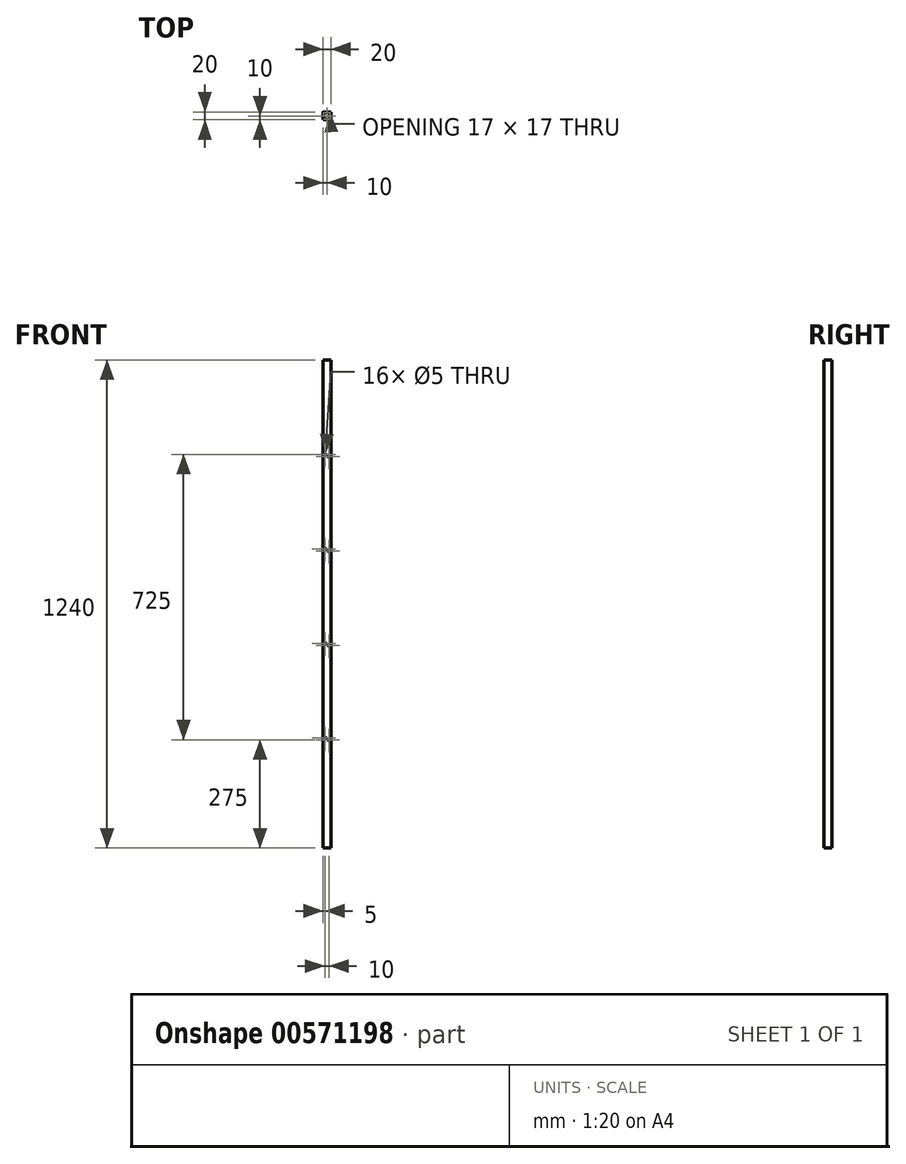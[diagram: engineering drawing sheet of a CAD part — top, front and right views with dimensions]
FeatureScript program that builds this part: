
annotation { "Feature Type Name" : "Feature", "Feature Type Description" : "" }
export const myFeature = defineFeature(function(context is Context, id is Id, definition is map)
    precondition{}
    {
        {
            var Q0;
            Q0=qCreatedBy(makeId("Top.planeOp"),FACE);
            var sketch = newSketch(context, id + "F0", { "sketchPlane" : qUnion([Q0])});
            skLineSegment(sketch, "E0.bottom", {"start": v(0, 0) * mm, "end": v(20, 0) * mm});
            skLineSegment(sketch, "E0.top", {"start": v(0.5, 20) * mm, "end": v(20, 20) * mm});
            skLineSegment(sketch, "E0.left", {"start": v(0, 0) * mm, "end": v(0, 19.5) * mm});
            skLineSegment(sketch, "E0.right", {"start": v(20, 0) * mm, "end": v(20, 20) * mm});
            skLineSegment(sketch, "E1.bottom", {"start": v(2, 18.5) * mm, "end": v(18, 18.5) * mm});
            skLineSegment(sketch, "E1.top", {"start": v(2, 1.5) * mm, "end": v(18, 1.5) * mm});
            skLineSegment(sketch, "E1.left", {"start": v(1.5, 18) * mm, "end": v(1.5, 2) * mm});
            skLineSegment(sketch, "E1.right", {"start": v(18.5, 18) * mm, "end": v(18.5, 2) * mm});
            skPoint(sketch, "E2.visualSharp", {"position": v(1.5, 18.5) * mm});
            skArc(sketch, "E2.filletArc", {"start": v(2, 18.5) * mm, "mid": v(1.65, 18.35) * mm, "end": v(1.5, 18) * mm});
            skPoint(sketch, "E3.visualSharp", {"position": v(1.5, 1.5) * mm});
            skArc(sketch, "E3.filletArc", {"start": v(1.5, 2) * mm, "mid": v(1.65, 1.65) * mm, "end": v(2, 1.5) * mm});
            skPoint(sketch, "E4.visualSharp", {"position": v(18.5, 1.5) * mm});
            skArc(sketch, "E4.filletArc", {"start": v(18, 1.5) * mm, "mid": v(18.35, 1.65) * mm, "end": v(18.5, 2) * mm});
            skPoint(sketch, "E5.visualSharp", {"position": v(18.5, 18.5) * mm});
            skArc(sketch, "E5.filletArc", {"start": v(18.5, 18) * mm, "mid": v(18.35, 18.35) * mm, "end": v(18, 18.5) * mm});
            skPoint(sketch, "E6.visualSharp", {"position": v(0, 20) * mm});
            skArc(sketch, "E6.filletArc", {"start": v(0.5, 20) * mm, "mid": v(0.15, 19.85) * mm, "end": v(0, 19.5) * mm});
            skSolve(sketch);
        }
        {
            var Q0;
            Q0=makeQuery(id+"F0.imprint","IMPRINT",FACE,{"disambiguationData":[TD([[makeQuery(id+"F0.imprint","IMPRINT",EDGE,{"derivedFrom":sQuery(id+"F0.wireOp",EDGE,"E0.bottom")}),1.0]])]});
            extrude(context, id + "F1", {"entities" : qUnion([Q0]), "depth" : 1240 * mm, "offsetDistance" : 25 * mm});
        }
        {
            var Q0;
            Q0=makeQuery(id+"F1.opExtrude","SWEPT_FACE",FACE,{"disambiguationData":[OSD([sQuery(id+"F0.wireOp",EDGE,"E0.bottom")])]});
            var sketch = newSketch(context, id + "F2", { "sketchPlane" : qUnion([Q0])});
            skPoint(sketch, "E7", {"position": v(5, 1000) * mm});
            skPoint(sketch, "E8", {"position": v(15, 995) * mm});
            skPoint(sketch, "E9.0.1.0", {"position": v(15, 755) * mm});
            skPoint(sketch, "E9.0.1.1", {"position": v(5, 760) * mm});
            skPoint(sketch, "E9.0.2.0", {"position": v(15, 515) * mm});
            skPoint(sketch, "E9.0.2.1", {"position": v(5, 520) * mm});
            skPoint(sketch, "E9.0.3.0", {"position": v(15, 275) * mm});
            skPoint(sketch, "E9.0.3.1", {"position": v(5, 280) * mm});
            skLineSegment(sketch, "E9.direction1", {"start": v(5, 1000) * mm, "end": v(30, 1000) * mm, "construction": true});
            skLineSegment(sketch, "E9.direction2", {"start": v(5, 1000) * mm, "end": v(5, 760) * mm, "construction": true});
            skSolve(sketch);
        }
        {
            var Q0;
            Q0=sQuery(id+"F2.wireOp",VERTEX,"E7");
            var Q1;
            Q1=sQuery(id+"F2.wireOp",VERTEX,"E8");
            var Q2;
            Q2=sQuery(id+"F2.wireOp",VERTEX,"E9.0.1.1");
            var Q3;
            Q3=sQuery(id+"F2.wireOp",VERTEX,"E9.0.1.0");
            var Q4;
            Q4=sQuery(id+"F2.wireOp",VERTEX,"E9.0.2.1");
            var Q5;
            Q5=sQuery(id+"F2.wireOp",VERTEX,"E9.0.2.0");
            var Q6;
            Q6=sQuery(id+"F2.wireOp",VERTEX,"E9.0.3.1");
            var Q7;
            Q7=sQuery(id+"F2.wireOp",VERTEX,"E9.0.3.0");
            var Q8;
            Q8=makeQuery(id+"F1.opExtrude","SWEPT_BODY",BODY,{"disambiguationData":[OSD([sQuery(id+"F0.wireOp",EDGE,"E0.bottom"),sQuery(id+"F0.wireOp",EDGE,"E0.top"),sQuery(id+"F0.wireOp",EDGE,"E0.left"),sQuery(id+"F0.wireOp",EDGE,"E0.right"),sQuery(id+"F0.wireOp",EDGE,"E1.bottom"),sQuery(id+"F0.wireOp",EDGE,"E1.top"),sQuery(id+"F0.wireOp",EDGE,"E1.left"),sQuery(id+"F0.wireOp",EDGE,"E1.right"),sQuery(id+"F0.wireOp",EDGE,"E2.filletArc"),sQuery(id+"F0.wireOp",EDGE,"E3.filletArc"),sQuery(id+"F0.wireOp",EDGE,"E4.filletArc"),sQuery(id+"F0.wireOp",EDGE,"E5.filletArc"),sQuery(id+"F0.wireOp",EDGE,"E6.filletArc")])]});
            hole(context, id + "F3", {"style" : HoleStyle.SIMPLE, "endStyle" : HoleEndStyle.THROUGH, "holeDiameter" : 5 * mm, "isTappedThrough" : true, "tappedDepth" : 12 * mm, "tapClearance" : 3, "locations" : qUnion([Q0, Q1, Q2, Q3, Q4, Q5, Q6, Q7]), "scope" : qUnion([Q8])});
        }
    });
